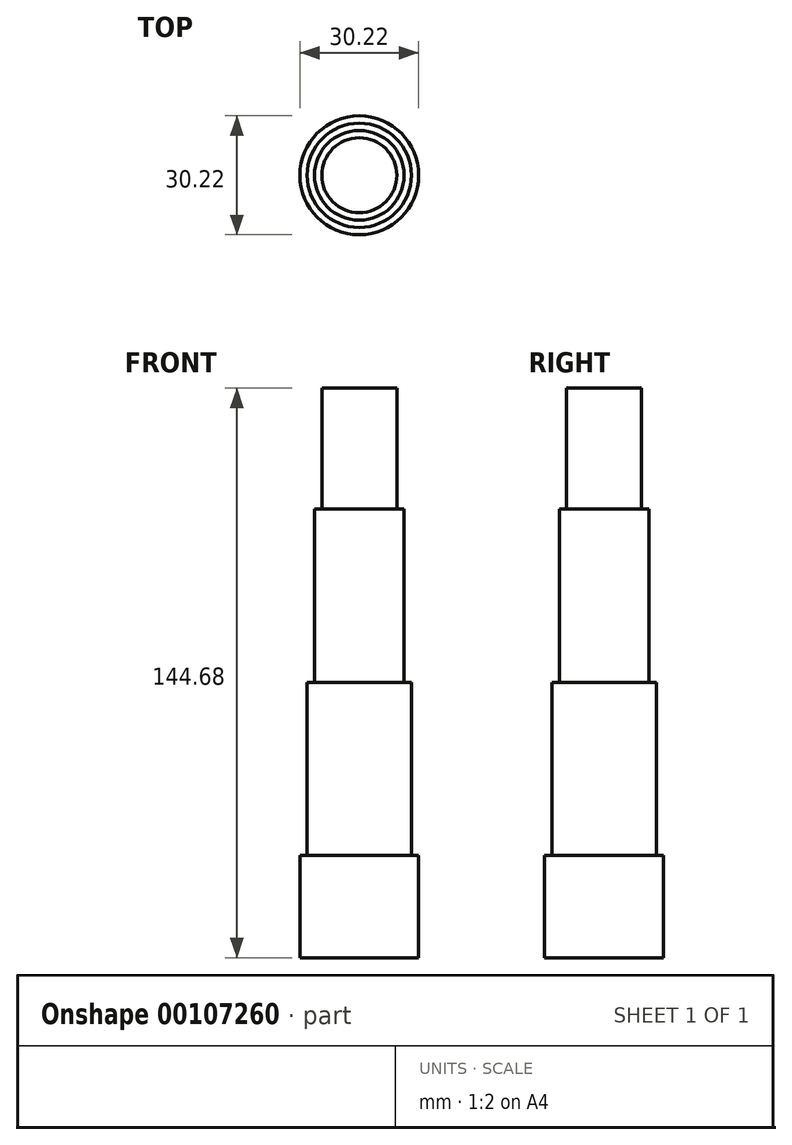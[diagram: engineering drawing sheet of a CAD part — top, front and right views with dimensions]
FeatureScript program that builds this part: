
annotation { "Feature Type Name" : "Feature", "Feature Type Description" : "" }
export const myFeature = defineFeature(function(context is Context, id is Id, definition is map)
    precondition{}
    {
        {
            var Q0;
            Q0=qCreatedBy(makeId("Front.planeOp"),FACE);
            var sketch = newSketch(context, id + "F0", { "sketchPlane" : qUnion([Q0])});
            skLineSegment(sketch, "E0", {"start": v(0, 0) * mm, "end": v(0, 109.86) * mm, "construction": true});
            skLineSegment(sketch, "E1.bottom", {"start": v(-15.1, 10.32) * mm, "end": v(-31.75, 10.32) * mm, "construction": true});
            skLineSegment(sketch, "E1.top", {"start": v(-15.1, -10.32) * mm, "end": v(-31.75, -10.32) * mm, "construction": true});
            skLineSegment(sketch, "E1.left", {"start": v(-15.1, 10.32) * mm, "end": v(-15.1, -10.32) * mm, "construction": true});
            skLineSegment(sketch, "E1.right", {"start": v(-31.75, 10.32) * mm, "end": v(-31.75, -10.32) * mm, "construction": true});
            skPoint(sketch, "E1.middle", {"position": v(-23.43, 0) * mm});
            skLineSegment(sketch, "E2.bottom", {"start": v(-9.52, 121.37) * mm, "end": v(-24.61, 121.37) * mm, "construction": true});
            skLineSegment(sketch, "E2.top", {"start": v(-9.52, 98.34) * mm, "end": v(-24.61, 98.34) * mm, "construction": true});
            skLineSegment(sketch, "E2.left", {"start": v(-9.53, 121.37) * mm, "end": v(-9.53, 98.34) * mm, "construction": true});
            skLineSegment(sketch, "E2.right", {"start": v(-24.61, 121.37) * mm, "end": v(-24.61, 98.34) * mm, "construction": true});
            skPoint(sketch, "E2.middle", {"position": v(-17.07, 109.86) * mm});
            skLineSegment(sketch, "E3", {"start": v(-9.53, 129.04) * mm, "end": v(-9.53, 98.34) * mm});
            skLineSegment(sketch, "E4", {"start": v(-11.39, 98.34) * mm, "end": v(-11.39, 54.33) * mm});
            skLineSegment(sketch, "E5", {"start": v(-11.39, 54.33) * mm, "end": v(-13.25, 54.33) * mm});
            skLineSegment(sketch, "E6", {"start": v(-13.25, 54.33) * mm, "end": v(-13.25, 10.32) * mm});
            skLineSegment(sketch, "E7", {"start": v(-15.1, 10.32) * mm, "end": v(-13.25, 10.32) * mm});
            skLineSegment(sketch, "E8", {"start": v(-11.39, 98.34) * mm, "end": v(-9.52, 98.34) * mm});
            skLineSegment(sketch, "E9", {"start": v(-15.1, 10.32) * mm, "end": v(-15.1, -15.64) * mm});
            skLineSegment(sketch, "E10", {"start": v(-9.53, 129.04) * mm, "end": v(0, 129.04) * mm});
            skLineSegment(sketch, "E11", {"start": v(0, 129.04) * mm, "end": v(0, -15.64) * mm});
            skLineSegment(sketch, "E12", {"start": v(0, -15.64) * mm, "end": v(-15.1, -15.64) * mm});
            skSolve(sketch);
        }
        {
            var Q0;
            Q0 = qSketchRegion(id + "F0", true);
            var Q1;
            Q1=sQuery(id+"F0.wireOp",EDGE,"E11");
            revolve(context, id + "F1", {"entities" : qUnion([Q0]), "axis" : qUnion([Q1]), "revolveType" : RevolveType.FULL});
        }
    });
